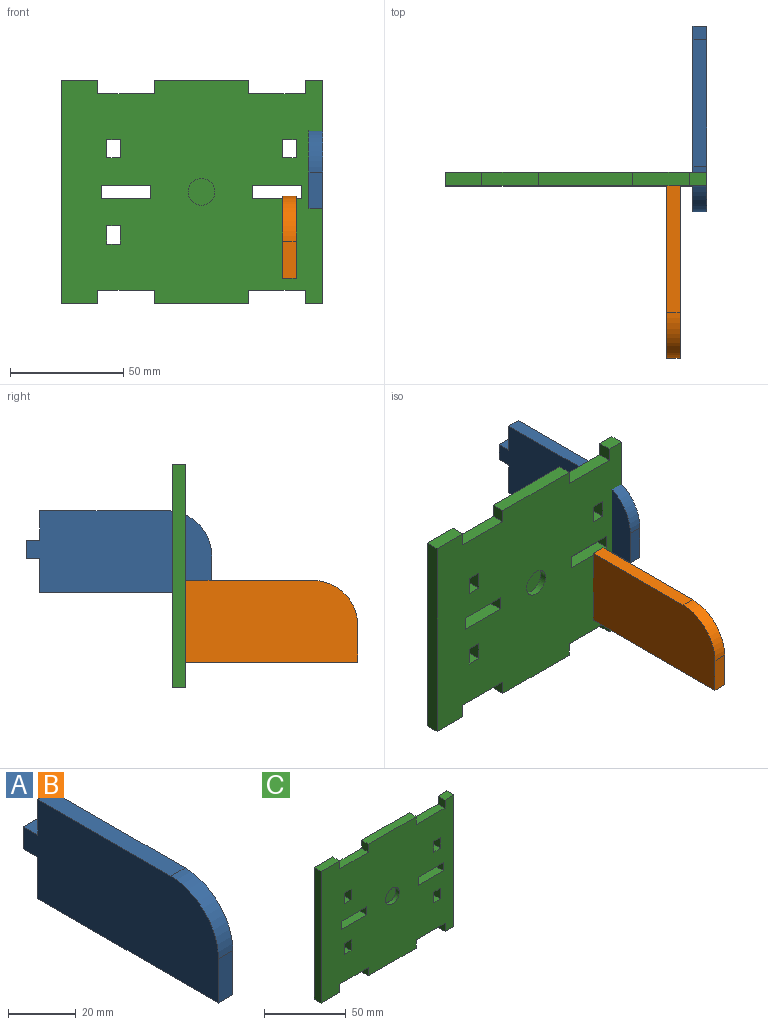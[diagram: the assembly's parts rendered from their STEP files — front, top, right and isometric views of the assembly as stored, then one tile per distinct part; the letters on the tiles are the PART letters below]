
ASSEMBLY  parts=3 mates=1
PART A: 11 faces, bbox 6x81.8x36 mm
  f0: plane 75.81x6mm, normal (0,0,-1), area 454.9mm2, adj f1,f8,f9,f10
  f1: plane 15x6mm, normal (0,1,0), area 90mm2, adj f0,f2,f9,f10
  f2: plane 6x6mm, normal (0,0,-1), area 36mm2, adj f1,f3,f9,f10
  f3: plane 8x6mm, normal (0,1,0), area 48mm2, adj f2,f4,f9,f10
  f4: plane 6x6mm, normal (0,0,1), area 36mm2, adj f3,f5,f9,f10
  f5: plane 13x6mm, normal (0,1,0), area 78mm2, adj f4,f6,f9,f10
  f6: plane 55.81x6mm, normal (0,0,1), area 334.9mm2, adj f5,f7,f9,f10
  f7: cylinder r=20mm len=20mm, axis (-1,0,0), area 188.5mm2, adj f6,f8,f9,f10
  f8: plane 16x6mm, normal (0,-1,0), area 96mm2, adj f0,f7,f9,f10
  f9: plane 81.81x36mm, normal (1,0,0), area 2691.4mm2, adj f0,f1,f2,f3,f4,f5,f6,f7
  f10: plane 81.81x36mm, normal (-1,0,0), area 2691.4mm2, adj f0,f1,f2,f3,f4,f5,f6,f7
PART B: same geometry as A
PART C: 48 faces, bbox 115x6x98.7 mm
  f0: plane 6x6mm, normal (0,0,1), area 36mm2, adj f1,f43,f44,f45
  f1: plane 8x6mm, normal (1,0,0), area 48mm2, adj f0,f2,f44,f45
  f2: plane 6x6mm, normal (0,0,-1), area 36mm2, adj f1,f43,f44,f45
  f3: plane 6.03x6mm, normal (1,0,0), area 36.2mm2, adj f4,f37,f44,f45
  f4: plane 21.94x6mm, normal (0,0,-1), area 131.6mm2, adj f3,f5,f44,f45
  f5: plane 6.03x6mm, normal (-1,0,0), area 36.2mm2, adj f4,f37,f44,f45
  f6: plane 6.03x6mm, normal (1,0,0), area 36.2mm2, adj f7,f38,f44,f45
  f7: plane 21.94x6mm, normal (0,0,-1), area 131.6mm2, adj f6,f8,f44,f45
  f8: plane 6.03x6mm, normal (-1,0,0), area 36.2mm2, adj f7,f38,f44,f45
  f9: plane 6x6mm, normal (0,0,1), area 36mm2, adj f10,f39,f44,f45
  f10: plane 8x6mm, normal (1,0,0), area 48mm2, adj f9,f11,f44,f45
  f11: plane 6x6mm, normal (0,0,-1), area 36mm2, adj f10,f39,f44,f45
  f12: plane 8x6mm, normal (1,0,0), area 48mm2, adj f13,f40,f44,f45
  f13: plane 6x6mm, normal (0,0,-1), area 36mm2, adj f12,f14,f44,f45
  f14: plane 8x6mm, normal (-1,0,0), area 48mm2, adj f13,f40,f44,f45
  f15: plane 8x6mm, normal (1,0,0), area 48mm2, adj f16,f41,f44,f45
  f16: plane 6x6mm, normal (0,0,-1), area 36mm2, adj f15,f17,f44,f45
  f17: plane 8x6mm, normal (-1,0,0), area 48mm2, adj f16,f41,f44,f45
  f18: plane 41.46x6mm, normal (0,0,1), area 248.8mm2, adj f19,f42,f44,f45
  f19: plane 6x6mm, normal (-1,0,0), area 36mm2, adj f18,f20,f44,f45
  f20: plane 25x6mm, normal (0,0,1), area 150mm2, adj f19,f21,f44,f45
  f21: plane 6x6mm, normal (1,0,0), area 36mm2, adj f20,f22,f44,f45
  f22: plane 16x6mm, normal (0,0,1), area 96mm2, adj f21,f23,f44,f45
  f23: plane 98.68x6mm, normal (-1,0,0), area 592.1mm2, adj f22,f24,f44,f45
  f24: plane 16x6mm, normal (0,0,-1), area 96mm2, adj f23,f25,f44,f45
  f25: plane 6.14x6mm, normal (1,0,0), area 36.8mm2, adj f24,f26,f44,f45
  f26: plane 25x6mm, normal (0,0,-1), area 150mm2, adj f25,f27,f44,f45
  f27: plane 6.14x6mm, normal (-1,0,0), area 36.8mm2, adj f26,f28,f44,f45
  f28: plane 41.46x6mm, normal (0,0,-1), area 248.8mm2, adj f27,f29,f44,f45
  f29: plane 6.14x6mm, normal (1,0,0), area 36.8mm2, adj f28,f30,f44,f45
  f30: plane 25x6mm, normal (0,0,-1), area 150mm2, adj f29,f31,f44,f45
  f31: plane 6.14x6mm, normal (-1,0,0), area 36.8mm2, adj f30,f32,f44,f45
  f32: plane 7.54x6mm, normal (0,0,-1), area 45.2mm2, adj f31,f33,f44,f45
  f33: plane 98.68x6mm, normal (1,0,0), area 592.1mm2, adj f32,f34,f44,f45
  f34: plane 7.54x6mm, normal (0,0,1), area 45.2mm2, adj f33,f35,f44,f45
  f35: plane 6x6mm, normal (-1,0,0), area 36mm2, adj f34,f36,f44,f45
  f36: plane 25x6mm, normal (0,0,1), area 150mm2, adj f35,f42,f44,f45
  f37: plane 21.94x6mm, normal (0,0,1), area 131.6mm2, adj f3,f5,f44,f45
  f38: plane 21.94x6mm, normal (0,0,1), area 131.6mm2, adj f6,f8,f44,f45
  f39: plane 8x6mm, normal (-1,0,0), area 48mm2, adj f9,f11,f44,f45
  f40: plane 6x6mm, normal (0,0,1), area 36mm2, adj f12,f14,f44,f45
  f41: plane 6x6mm, normal (0,0,1), area 36mm2, adj f15,f17,f44,f45
  f42: plane 6x6mm, normal (1,0,0), area 36mm2, adj f18,f36,f44,f45
  f43: plane 8x6mm, normal (-1,0,0), area 48mm2, adj f0,f2,f44,f45
  f44: plane 115x98.68mm, normal (0,-1,0), area 10174.2mm2, adj f0,f1,f2,f3,f4,f5,f6,f7
  f45: plane 115x98.68mm, normal (0,1,0), area 10284.8mm2, adj f0,f1,f2,f3,f4,f5,f6,f7
  f46: cylinder r=5.93mm len=11.87mm, axis (0,-1,0), area 111.9mm2, adj f44,f47
  f47: plane 11.87x11.87mm, normal (0,-1,0), area 110.6mm2, adj f46
PLACE A t=(39.1,51.7,-10.98)mm
PLACE B t=(27.48,-12.72,-41.69)mm
PLACE C t=(-8.26,-6.72,-3.69)mm
MATE planar B.f2 <-> C.f0  axis (0,0,-1) through (30.48,-9.72,-26.69)mm
